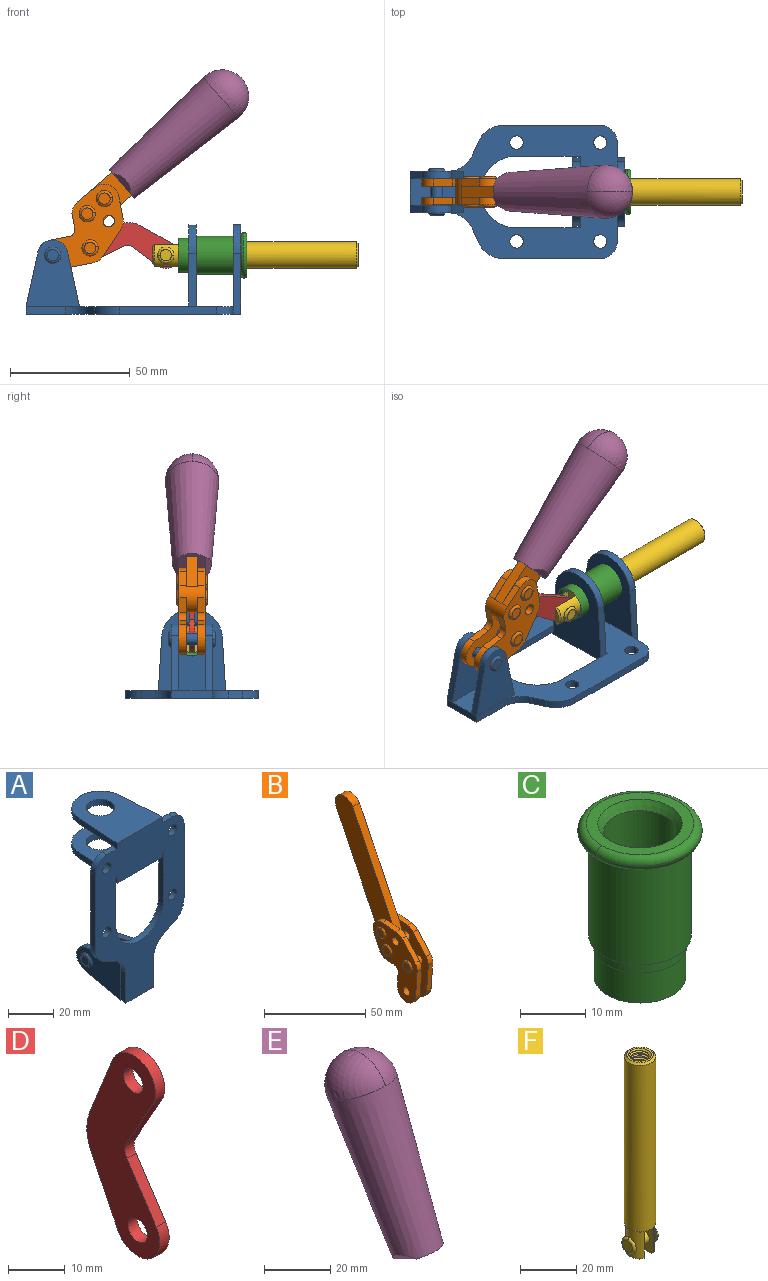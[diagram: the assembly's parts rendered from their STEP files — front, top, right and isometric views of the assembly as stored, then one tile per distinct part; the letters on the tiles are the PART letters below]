
ASSEMBLY  parts=6 mates=6
PART A: 55 faces, bbox 55.7x37.4x89.8 mm
  f0: torus R=2.41mm, axis (-1,0,0), area 15mm2, adj f11,f15,f25
  f1: torus R=2.41mm, axis (-1,0,0), area 15mm2, adj f10,f12,f22
  f2: cylinder r=2.78mm len=5.56mm, axis (0,-1,0), area 54.2mm2, adj f30,f54
  f3: cylinder r=14.99mm len=29.97mm, axis (0,-1,0), area 145.9mm2, adj f30,f49,f53,f54
  f4: cylinder r=2.78mm len=5.56mm, axis (0,-1,0), area 54.2mm2, adj f30,f54
  f5: cylinder r=2.78mm len=5.56mm, axis (0,-1,0), area 54.2mm2, adj f30,f54
  f6: cylinder r=2.78mm len=5.56mm, axis (0,-1,0), area 54.2mm2, adj f30,f54
  f7: cylinder r=6.35mm len=12.7mm, axis (0,0,1), area 123.6mm2, adj f27,f51
  f8: cylinder r=6.35mm len=12.7mm, axis (0,0,-1), area 124.7mm2, adj f21,f35
  f9: cylinder r=2.41mm len=11.18mm, axis (-1,0,0), area 169.4mm2, adj f16,f19
  f10: plane 4.83x4.83mm, normal (1,0,0), area 18.3mm2, adj f1,f12
  f11: plane 4.83x4.83mm, normal (-1,0,0), area 18.3mm2, adj f0,f15
  f12: torus R=2.41mm, axis (-1,0,0), area 15mm2, adj f1,f10,f22
  f13: cylinder r=6.35mm len=12.41mm, axis (1,0,0), area 53.4mm2, adj f18,f19,f22,f23
  f14: cylinder r=6.35mm len=12.41mm, axis (-1,0,0), area 53.4mm2, adj f16,f17,f24,f25
  f15: torus R=2.41mm, axis (-1,0,0), area 15mm2, adj f0,f11,f25
  f16: plane 27.86x22.35mm, normal (1,0,0), area 425.4mm2, adj f9,f14,f17,f24,f30
  f17: plane 22.86x4.97mm, normal (0,0.21,0.98), area 72.5mm2, adj f14,f16,f25,f30
  f18: plane 22.86x4.97mm, normal (0,0.21,0.98), area 72.5mm2, adj f13,f19,f22,f30
  f19: plane 27.86x22.35mm, normal (-1,0,0), area 425.4mm2, adj f9,f13,f18,f23,f30
  f20: cylinder r=12.7mm len=25.35mm, axis (0,0,-1), area 119.8mm2, adj f21,f34,f35,f36
  f21: plane 34.21x28.07mm, normal (0,0,-1), area 702.4mm2, adj f8,f20,f30,f34,f36
  f22: plane 27.96x22.45mm, normal (1,0,0), area 407.2mm2, adj f1,f12,f13,f18,f23,f30,f42,f43
  f23: plane 22.86x4.97mm, normal (0,0.21,-0.98), area 72.5mm2, adj f13,f19,f22,f44
  f24: plane 22.86x4.97mm, normal (0,0.21,-0.98), area 72.5mm2, adj f14,f16,f25,f44
  f25: plane 27.86x22.35mm, normal (-1,0,0), area 407.1mm2, adj f0,f14,f15,f17,f24,f30,f45,f46
  f26: plane 3.1x0.95mm, normal (0,0,-1), area 2.7mm2, adj f30,f49,f50,f54
  f27: plane 34.21x28.07mm, normal (0,0,1), area 702.4mm2, adj f7,f28,f30,f50,f52
  f28: cylinder r=12.7mm len=25.35mm, axis (0,0,1), area 118.8mm2, adj f27,f50,f51,f52
  f29: plane 3.1x0.95mm, normal (0,0,-1), area 2.7mm2, adj f30,f52,f53,f54
  f30: plane 86.54x55.63mm, normal (0,1,0), area 2362.9mm2, adj f2,f3,f4,f5,f6,f16,f17,f18
  f31: plane 40.56x3.1mm, normal (-1,0,0), area 125.7mm2, adj f30,f32,f48,f54
  f32: cylinder r=7.11mm len=7.11mm, axis (0,-1,0), area 34.6mm2, adj f30,f31,f33,f54
  f33: plane 6.67x3.1mm, normal (0,0,1), area 20.4mm2, adj f30,f32,f34,f54
  f34: plane 25.39x3.13mm, normal (-1,0.06,0), area 79.5mm2, adj f20,f21,f33,f35,f54
  f35: plane 37.31x28.45mm, normal (0,0,1), area 789.9mm2, adj f8,f20,f34,f36,f54
  f36: plane 25.39x3.13mm, normal (1,0.06,0), area 79.5mm2, adj f20,f21,f35,f37,f54
  f37: plane 6.67x3.1mm, normal (0,0,1), area 20.4mm2, adj f30,f36,f38,f54
  f38: cylinder r=7.11mm len=7.11mm, axis (0,-1,0), area 34.6mm2, adj f30,f37,f39,f54
  f39: plane 40.56x3.1mm, normal (1,0,0), area 125.7mm2, adj f30,f38,f40,f54
  f40: cylinder r=11.18mm len=10.16mm, axis (0,-1,0), area 39.5mm2, adj f30,f39,f41,f54
  f41: plane 6.09x3.1mm, normal (0.42,0,-0.91), area 20.8mm2, adj f30,f40,f42,f54
  f42: cylinder r=11.18mm len=9.41mm, axis (0,-1,0), area 37.2mm2, adj f22,f30,f41,f43,f54
  f43: plane 16.5x3.1mm, normal (1,0,0), area 51.1mm2, adj f22,f42,f44,f54
  f44: plane 17.37x3.1mm, normal (0,0,-1), area 53.8mm2, adj f23,f24,f30,f43,f45,f54
  f45: plane 16.5x3.1mm, normal (-1,0,0), area 51.1mm2, adj f25,f44,f46,f54
  f46: cylinder r=11.18mm len=9.41mm, axis (0,-1,0), area 37.2mm2, adj f25,f30,f45,f47,f54
  f47: plane 6.09x3.1mm, normal (-0.42,0,-0.91), area 20.8mm2, adj f30,f46,f48,f54
  f48: cylinder r=11.18mm len=10.16mm, axis (0,-1,0), area 39.5mm2, adj f30,f31,f47,f54
  f49: plane 26.54x3.1mm, normal (-1,0,0), area 82.3mm2, adj f3,f26,f30,f54
  f50: plane 25.39x3.1mm, normal (1,0.06,0), area 78.8mm2, adj f26,f27,f28,f51,f54
  f51: plane 37.31x28.45mm, normal (0,0,-1), area 789.9mm2, adj f7,f28,f50,f52,f54
  f52: plane 25.39x3.1mm, normal (-1,0.06,0), area 78.8mm2, adj f27,f28,f29,f51,f54
  f53: plane 26.54x3.1mm, normal (1,0,0), area 82.3mm2, adj f3,f29,f30,f54
  f54: plane 89.66x55.63mm, normal (0,-1,0), area 2678.5mm2, adj f2,f3,f4,f5,f6,f26,f29,f31
PART B: 59 faces, bbox 12.9x60.2x99.6 mm
  f0: torus R=2.39mm, axis (-1,0,0), area 14.9mm2, adj f20,f43,f51
  f1: torus R=2.39mm, axis (-1,0,0), area 14.9mm2, adj f19,f42,f51
  f2: torus R=2.39mm, axis (-1,0,0), area 14.9mm2, adj f18,f35,f51
  f3: torus R=2.39mm, axis (-1,0,0), area 14.9mm2, adj f14,f17,f23
  f4: torus R=2.39mm, axis (-1,0,0), area 14.9mm2, adj f13,f16,f23
  f5: torus R=2.39mm, axis (-1,0,0), area 14.9mm2, adj f12,f15,f23
  f6: cylinder r=2.39mm len=4.78mm, axis (1,0,0), area 46.5mm2, adj f48,f50,f51
  f7: cylinder r=2.39mm len=4.78mm, axis (1,0,0), area 46.5mm2, adj f50,f51
  f8: cylinder r=6.35mm len=12.68mm, axis (1,0,0), area 61.8mm2, adj f38,f39,f50,f51
  f9: cylinder r=2.39mm len=4.78mm, axis (-1,0,0), area 70.5mm2, adj f46,f50
  f10: cylinder r=2.39mm len=4.78mm, axis (-1,0,0), area 46.5mm2, adj f23,f45,f46
  f11: cylinder r=2.39mm len=4.78mm, axis (-1,0,0), area 46.5mm2, adj f23,f46
  f12: plane 4.78x4.78mm, normal (1,0,0), area 17.9mm2, adj f5,f15
  f13: plane 4.78x4.78mm, normal (1,0,0), area 17.9mm2, adj f4,f16
  f14: plane 4.78x4.78mm, normal (1,0,0), area 17.9mm2, adj f3,f17
  f15: torus R=2.39mm, axis (-1,0,0), area 14.9mm2, adj f5,f12,f23
  f16: torus R=2.39mm, axis (-1,0,0), area 14.9mm2, adj f4,f13,f23
  f17: torus R=2.39mm, axis (-1,0,0), area 14.9mm2, adj f3,f14,f23
  f18: plane 4.78x4.78mm, normal (-1,0,0), area 17.9mm2, adj f2,f35
  f19: plane 4.78x4.78mm, normal (-1,0,0), area 17.9mm2, adj f1,f42
  f20: plane 4.78x4.78mm, normal (-1,0,0), area 17.9mm2, adj f0,f43
  f21: plane 2.26x0.2mm, normal (1,0,0), area 0.2mm2, adj f31,f44
  f22: plane 2.26x0.2mm, normal (-1,0,0), area 0.2mm2, adj f41,f44
  f23: plane 39.37x30.77mm, normal (1,0,0), area 565.5mm2, adj f3,f4,f5,f10,f11,f15,f16,f17
  f24: cylinder r=6.1mm len=4.15mm, axis (-1,0,0), area 14.7mm2, adj f23,f25,f32,f46
  f25: plane 10.25x9.01mm, normal (0,-0.75,0.66), area 42.3mm2, adj f23,f24,f26,f46
  f26: cylinder r=6.35mm len=4.64mm, axis (-1,0,0), area 15.6mm2, adj f23,f25,f27,f46
  f27: plane 15.84x3.1mm, normal (0,-1,-0.07), area 49.2mm2, adj f23,f26,f28,f46
  f28: cylinder r=6.35mm len=12.68mm, axis (-1,0,0), area 61.8mm2, adj f23,f27,f29,f46
  f29: plane 8.11x3.1mm, normal (0,1,0.07), area 25.2mm2, adj f23,f28,f30,f46
  f30: cylinder r=3.05mm len=3.25mm, axis (-1,0,0), area 14.8mm2, adj f23,f29,f31,f46
  f31: plane 5.99x3.1mm, normal (0,0.07,-1), area 18.6mm2, adj f21,f23,f30,f44,f46
  f32: plane 9.5x3.1mm, normal (0,-0.07,1), area 29.5mm2, adj f23,f24,f33,f46,f47
  f33: cylinder r=6.1mm len=8.63mm, axis (-1,0,0), area 39.1mm2, adj f23,f32,f34,f47
  f34: plane 8.65x3.96mm, normal (0,0.91,-0.42), area 29.5mm2, adj f23,f33,f44,f47
  f35: torus R=2.39mm, axis (-1,0,0), area 14.9mm2, adj f2,f18,f51
  f36: plane 10.25x9.01mm, normal (0,-0.75,0.66), area 42.3mm2, adj f37,f49,f50,f51
  f37: cylinder r=6.35mm len=4.64mm, axis (1,0,0), area 15.6mm2, adj f36,f38,f50,f51
  f38: plane 15.84x3.1mm, normal (0,-1,-0.07), area 49.2mm2, adj f8,f37,f50,f51
  f39: plane 8.11x3.1mm, normal (0,1,0.07), area 25.2mm2, adj f8,f40,f50,f51
  f40: cylinder r=3.05mm len=3.25mm, axis (1,0,0), area 14.8mm2, adj f39,f41,f50,f51
  f41: plane 5.99x3.1mm, normal (0,0.07,-1), area 18.6mm2, adj f22,f40,f44,f50,f51
  f42: torus R=2.39mm, axis (-1,0,0), area 14.9mm2, adj f1,f19,f51
  f43: torus R=2.39mm, axis (-1,0,0), area 14.9mm2, adj f0,f20,f51
  f44: cylinder r=6.35mm len=12.12mm, axis (-1,0,0), area 128.9mm2, adj f21,f22,f23,f31,f34,f41,f46,f47
  f45: plane 2.65x1.35mm, normal (1,0,0), area 1mm2, adj f10,f55
  f46: plane 39.08x20.42mm, normal (-1,0,0), area 412.5mm2, adj f9,f10,f11,f24,f25,f26,f27,f28
  f47: plane 77.62x39.82mm, normal (1,0,0), area 850mm2, adj f32,f33,f34,f44,f53,f54,f55
  f48: plane 2.65x1.35mm, normal (-1,0,0), area 1mm2, adj f6,f55
  f49: cylinder r=6.1mm len=4.15mm, axis (1,0,0), area 14.7mm2, adj f36,f50,f51,f56
  f50: plane 39.08x20.42mm, normal (1,0,0), area 412.5mm2, adj f6,f7,f8,f9,f36,f37,f38,f39
  f51: plane 39.37x30.77mm, normal (-1,0,0), area 565.5mm2, adj f0,f1,f2,f6,f7,f8,f35,f36
  f52: plane 8.65x3.96mm, normal (0,0.91,-0.42), area 29.5mm2, adj f44,f51,f57,f58
  f53: plane 68.49x33.4mm, normal (0,0.9,-0.44), area 358.1mm2, adj f44,f47,f54,f58
  f54: cylinder r=6.35mm len=12.06mm, axis (1,0,0), area 93.7mm2, adj f47,f53,f55,f58
  f55: plane 68.49x33.4mm, normal (0,-0.9,0.44), area 358.1mm2, adj f44,f45,f46,f47,f48,f50,f54,f58
  f56: plane 9.5x3.1mm, normal (0,-0.07,1), area 29.5mm2, adj f49,f50,f51,f57,f58
  f57: cylinder r=6.1mm len=8.63mm, axis (1,0,0), area 39.1mm2, adj f51,f52,f56,f58
  f58: plane 77.62x39.82mm, normal (-1,0,0), area 850mm2, adj f44,f52,f53,f54,f55,f56,f57
PART C: 15 faces, bbox 20.6x20.6x28.7 mm
  f0: torus R=8.26mm, axis (0,0,1), area 56.8mm2, adj f1,f10,f12
  f1: torus R=8.26mm, axis (0,0,1), area 56.8mm2, adj f0,f6,f13
  f2: cylinder r=5.59mm len=25.91mm, axis (0,0,1), area 909.6mm2, adj f3,f4
  f3: cone r=6.86mm half-angle=45deg, axis (0,0,-1), area 70.2mm2, adj f2,f14
  f4: cone r=6.47mm half-angle=30deg, axis (0,0,1), area 66.7mm2, adj f2,f13
  f5: cylinder r=7.04mm len=14.07mm, axis (0,0,1), area 252.6mm2, adj f11,f14
  f6: torus R=8.26mm, axis (0,0,1), area 56.8mm2, adj f1,f12,f13
  f7: cylinder r=7.16mm len=14.33mm, axis (0,0,1), area 91.5mm2, adj f9,f11
  f8: cylinder r=7.86mm len=18.42mm, axis (0,0,1), area 909.6mm2, adj f9,f10
  f9: plane 15.72x15.72mm, normal (0,0,-1), area 33mm2, adj f7,f8
  f10: plane 16.51x16.51mm, normal (0,0,-1), area 19.9mm2, adj f0,f8,f12
  f11: plane 14.33x14.33mm, normal (0,0,-1), area 5.7mm2, adj f5,f7
  f12: torus R=8.26mm, axis (0,0,1), area 56.8mm2, adj f0,f6,f10
  f13: plane 16.51x16.51mm, normal (0,0,1), area 82.7mm2, adj f1,f4,f6
  f14: plane 14.07x14.07mm, normal (0,0,-1), area 7.8mm2, adj f3,f5
PART D: 12 faces, bbox 2.3x18.2x42.8 mm
  f0: cylinder r=2.4mm len=4.8mm, axis (1,0,0), area 34.9mm2, adj f4,f11
  f1: cylinder r=10.41mm len=8.47mm, axis (1,0,0), area 20.2mm2, adj f4,f9,f10,f11
  f2: cylinder r=3.05mm len=3.16mm, axis (1,0,0), area 7.7mm2, adj f4,f6,f7,f11
  f3: cylinder r=2.4mm len=4.8mm, axis (1,0,0), area 34.9mm2, adj f4,f11
  f4: plane 42.81x18.23mm, normal (-1,0,0), area 414.1mm2, adj f0,f1,f2,f3,f5,f6,f7,f8
  f5: cylinder r=5.54mm len=10.67mm, axis (1,0,0), area 41.8mm2, adj f4,f6,f10,f11
  f6: plane 11.66x6.53mm, normal (0,-0.87,-0.49), area 30.9mm2, adj f2,f4,f5,f11
  f7: plane 11.17x7.33mm, normal (0,-0.84,0.55), area 30.9mm2, adj f2,f4,f8,f11
  f8: cylinder r=5.54mm len=10.51mm, axis (1,0,0), area 41.8mm2, adj f4,f7,f9,f11
  f9: plane 13.67x6.67mm, normal (0,0.9,-0.44), area 35.1mm2, adj f1,f4,f8,f11
  f10: plane 14.1x5.7mm, normal (0,0.93,0.37), area 35.1mm2, adj f1,f4,f5,f11
  f11: plane 42.81x18.23mm, normal (1,0,0), area 414.1mm2, adj f0,f1,f2,f3,f5,f6,f7,f8
PART E: 11 faces, bbox 22.3x42.6x64.5 mm
  f0: sphere r=11.13mm, area 411.4mm2, adj f1,f8
  f1: cone r=11.11mm half-angle=3.3deg, axis (0,0.44,0.9), area 3251.8mm2, adj f0,f7,f8,f9,f10
  f2: cylinder r=6.16mm len=11.7mm, axis (1,0,0), area 89.5mm2, adj f3,f4,f5,f6
  f3: plane 60.23x36.75mm, normal (-1,0,0), area 763.6mm2, adj f2,f4,f6,f10
  f4: plane 51.37x25.05mm, normal (0,0.9,-0.44), area 264.2mm2, adj f2,f3,f5,f10
  f5: plane 60.23x36.75mm, normal (1,0,0), area 763.6mm2, adj f2,f4,f6,f10
  f6: plane 51.37x25.05mm, normal (0,-0.9,0.44), area 264.2mm2, adj f2,f3,f5,f10
  f7: plane 9.95x5.95mm, normal (0.71,-0.31,-0.64), area 25.8mm2, adj f1,f10
  f8: sphere r=11.13mm, area 411.4mm2, adj f0,f1
  f9: plane 9.95x5.95mm, normal (-0.71,-0.31,-0.64), area 25.8mm2, adj f1,f10
  f10: plane 14.27x11.38mm, normal (0,-0.44,-0.9), area 106.7mm2, adj f1,f3,f4,f5,f6,f7,f9
PART F: 48 faces, bbox 12.6x11.1x86.1 mm
  f0: torus R=2.41mm, axis (-1,0,0), area 15mm2, adj f30,f32,f34
  f1: torus R=2.41mm, axis (-1,0,0), area 15mm2, adj f29,f31,f33
  f2: cylinder r=5.54mm len=72.39mm, axis (0,0,1), area 2518.5mm2, adj f3,f4,f42,f43
  f3: cone r=5.54mm half-angle=45deg, axis (0,0,1), area 7.6mm2, adj f2,f5,f41
  f4: cone r=5.54mm half-angle=45deg, axis (0,0,-1), area 34.9mm2, adj f2,f39
  f5: cylinder r=5.08mm len=11.48mm, axis (0,0,1), area 108.3mm2, adj f3,f7,f8,f41
  f6: cylinder r=2.41mm len=4.83mm, axis (-1,0,0), area 71.2mm2, adj f40,f41
  f7: cylinder r=2.41mm len=4.83mm, axis (-1,0,0), area 7.6mm2, adj f5,f34
  f8: cone r=5.08mm half-angle=45deg, axis (0,0,1), area 10.6mm2, adj f5,f37,f41
  f9: cone r=3.98mm half-angle=45deg, axis (0,0,1), area 17.6mm2, adj f27,f39,f45,f46,f47
  f10: cylinder r=2.41mm len=4.83mm, axis (-1,0,0), area 7.6mm2, adj f33,f38
  f11: cylinder r=3.2mm len=6.4mm, axis (0,0,1), area 78.4mm2, adj f12,f28,f44,f45,f47
  f12: cylinder r=3.2mm len=6.4mm, axis (0,0,1), area 10.5mm2, adj f11,f13,f45,f47
  f13: cylinder r=3.2mm len=6.4mm, axis (0,0,1), area 10.5mm2, adj f12,f14,f45,f47
  f14: cylinder r=3.2mm len=6.4mm, axis (0,0,1), area 10.5mm2, adj f13,f15,f45,f47
  f15: cylinder r=3.2mm len=6.4mm, axis (0,0,1), area 10.5mm2, adj f14,f16,f45,f47
  f16: cylinder r=3.2mm len=6.4mm, axis (0,0,1), area 10.5mm2, adj f15,f17,f45,f47
  f17: cylinder r=3.2mm len=6.4mm, axis (0,0,1), area 10.5mm2, adj f16,f18,f45,f47
  f18: cylinder r=3.2mm len=6.4mm, axis (0,0,1), area 10.5mm2, adj f17,f19,f45,f47
  f19: cylinder r=3.2mm len=6.4mm, axis (0,0,1), area 10.5mm2, adj f18,f20,f45,f47
  f20: cylinder r=3.2mm len=6.4mm, axis (0,0,1), area 10.5mm2, adj f19,f21,f45,f47
  f21: cylinder r=3.2mm len=6.4mm, axis (0,0,1), area 10.5mm2, adj f20,f22,f45,f47
  f22: cylinder r=3.2mm len=6.4mm, axis (0,0,1), area 10.5mm2, adj f21,f23,f45,f47
  f23: cylinder r=3.2mm len=6.4mm, axis (0,0,1), area 10.5mm2, adj f22,f24,f45,f47
  f24: cylinder r=3.2mm len=6.4mm, axis (0,0,1), area 10.5mm2, adj f23,f25,f45,f47
  f25: cylinder r=3.2mm len=6.4mm, axis (0,0,1), area 10.5mm2, adj f24,f26,f45,f47
  f26: cylinder r=3.2mm len=6.4mm, axis (0,0,1), area 10.5mm2, adj f25,f27,f45,f47
  f27: cylinder r=3.2mm len=6.4mm, axis (0,0,1), area 7.4mm2, adj f9,f26,f45,f47
  f28: cone r=3.2mm half-angle=60deg, axis (0,0,1), area 37.2mm2, adj f11
  f29: plane 4.83x4.83mm, normal (-1,0,0), area 18.3mm2, adj f1,f31
  f30: plane 4.83x4.83mm, normal (1,0,0), area 18.3mm2, adj f0,f32
  f31: torus R=2.41mm, axis (-1,0,0), area 15mm2, adj f1,f29,f33
  f32: torus R=2.41mm, axis (-1,0,0), area 15mm2, adj f0,f30,f34
  f33: plane 6.83x6.83mm, normal (1,0,0), area 18.3mm2, adj f1,f10,f31
  f34: plane 6.83x6.83mm, normal (-1,0,0), area 18.3mm2, adj f0,f7,f32
  f35: cone r=5.08mm half-angle=45deg, axis (0,0,1), area 10.6mm2, adj f36,f38,f40
  f36: plane 7.25x1.97mm, normal (0,0,-1), area 10mm2, adj f35,f40
  f37: plane 7.25x1.97mm, normal (0,0,-1), area 10mm2, adj f8,f41
  f38: cylinder r=5.08mm len=11.48mm, axis (0,0,1), area 108.3mm2, adj f10,f35,f40,f42
  f39: plane 9.55x9.55mm, normal (0,0,1), area 22mm2, adj f4,f9
  f40: plane 12.76x10.09mm, normal (1,0,0), area 95.7mm2, adj f6,f35,f36,f38,f42,f43
  f41: plane 12.76x10.09mm, normal (-1,0,0), area 95.7mm2, adj f3,f5,f6,f8,f37,f43
  f42: cone r=5.54mm half-angle=45deg, axis (0,0,1), area 7.6mm2, adj f2,f38,f40
  f43: plane 11.07x4.7mm, normal (0,0,-1), area 50.4mm2, adj f2,f40,f41
  f44: plane 0.89x0.62mm, normal (-1,0,0), area 0.3mm2, adj f11,f45,f46,f47
  f45: bspline ~24.8x7.63mm, area 266.6mm2, adj f9,f11,f12,f13,f14,f15,f16,f17
  f46: bspline ~24.87x7.63mm, area 73.6mm2, adj f9,f44,f45,f47
  f47: bspline ~24.98x7.63mm, area 272.5mm2, adj f9,f11,f12,f13,f14,f15,f16,f17
PLACE A rot(axis=(0.58,0.58,0.58),120deg) t=(0,0,0)mm fixed
PLACE B rot(axis=(0.52,0.52,0.68),111.8deg) t=(5.28,0,9.14)mm
PLACE C rot(axis=(0,1,0),90deg) t=(0,-24.61,24.61)mm
PLACE D rot(axis=(0.57,-0.57,-0.6),118deg) t=(-2.56,0,2.14)mm
PLACE E rot(axis=(0.52,0.52,0.68),111.8deg) t=(5.28,-0.04,9.14)mm
PLACE F rot(axis=(-0.58,0.58,-0.58),120deg) t=(-0.38,0,49.23)mm
MATE fastened C.f0 <-> A.f7  axis (-1,0,0) through (46.39,0,24.61)mm
MATE fastened E.f2 <-> B.f54  axis (0,1,0) through (39.8,-2.35,91.94)mm
MATE revolute D.f3 <-> F.f6  axis (0,-1,0) through (15.1,0,24.61)mm
MATE revolute B.f7 <-> A.f0  axis (0,1,0) through (-32.09,0,24.61)mm
MATE slider F.f2 <-> C.f2  axis (1,0,0) through (58.4,0,24.61)mm
MATE revolute D.f5 <-> B.f4  axis (0,-1,0) through (-16.51,0,27.64)mm
